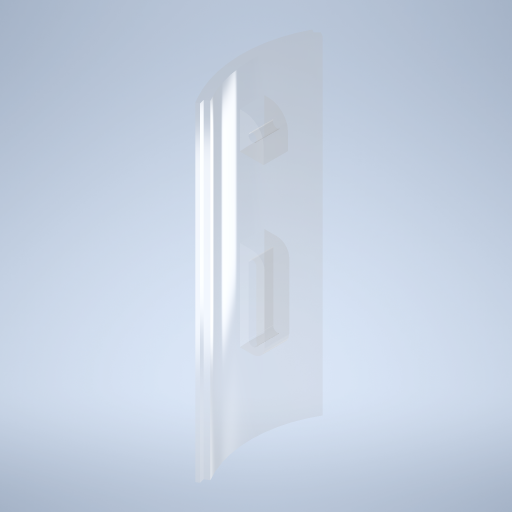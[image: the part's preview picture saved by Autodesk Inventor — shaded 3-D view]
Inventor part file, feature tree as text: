
AUTODESK INVENTOR PART (.ipt)
format: ipt  version: 2024.3 (Build 283343000, 343)  size: 366,080 bytes
history: native  units: mm
features: sketch x8, extrude x5, other x3, projected_geometry x3, plane x2, fillet x2, hole x2
ambient origin geometry x8: Origin, YZ Plane, XZ Plane, XY Plane, X Axis, Y Axis, Z Axis, Center Point
bodies: Body1 (feature_tree)
feature tree (25):
  other  "Sólido1"
  extrude  "Extrusión1"  Depth=152.4mm TaperAngle=0.0deg
  other  "Labio1"
  other  "Labio2"
  plane  "Plano de trabajo2"
  extrude  "Extrusión2"  Depth=15.0mm
  fillet  "Empalme1"  Radius=10.0mm
  plane  "Plano de trabajo3"
  extrude  "Extrusión4"  Depth=8.0mm
  fillet  "Empalme2"  Radius=4.5mm
  sketch  "Boceto4"  dims[d30=8.0mm d32=3.0mm d33=4.5mm]
  extrude  "Extrusión5"  Depth=10.0mm
  extrude  "Extrusión6"  Depth=5.0mm
  hole  "Agujero1"  [1 undecoded]
  hole  "Agujero5"  [1 undecoded]
  sketch  "Boceto1"  dims[d1=30.0deg d3=152.4mm d4=0.0mm]
  sketch  "Boceto3"  dims[d5=2.0mm d6=2.0mm d7=0.0mm d8=0.0mm d9=15.0deg d10=0.0mm d11=2.0mm d12=2.0mm d13=0.0mm d14=0.0mm d15=15.0deg d16=0.0mm d26=15.0mm d28=10.0mm d29=0.0mm]
  projected_geometry  "Contorno proyectado2"
  projected_geometry  "Contorno proyectado3"
  sketch  "Boceto5"  dims[d37=10.0mm d38=53.0mm]
  sketch  "Boceto6"  dims[d39=10.5mm d40=0.0mm d41=5.0mm]
  sketch  "Boceto7"  dims[d43=3.15mm d44=10.0mm d45=0.0mm]
  projected_geometry  "Contorno proyectado4"
  sketch  "Boceto8"  dims[d46=130.0mm d47=90.0mm]
  sketch  "Boceto12"  dims[d48=17.701mm d49=0.0mm d51=3.4mm d52=6.0mm d53=6.3mm d54=2.0mm d55=90.0deg d56=8.0mm d57=20.594885mm d80=3.4mm d81=6.0mm d82=4.0mm d83=2.0mm d84=90.0deg d85=8.0mm d86=0.0mm d34=0.0mm d35=0.0mm d50=0.0mm]
note: 2 required parameter values undecoded (feature->parameter linkage not recoverable at this tier; creation-order binding heuristic only, values carry confidence <= 0.55)
